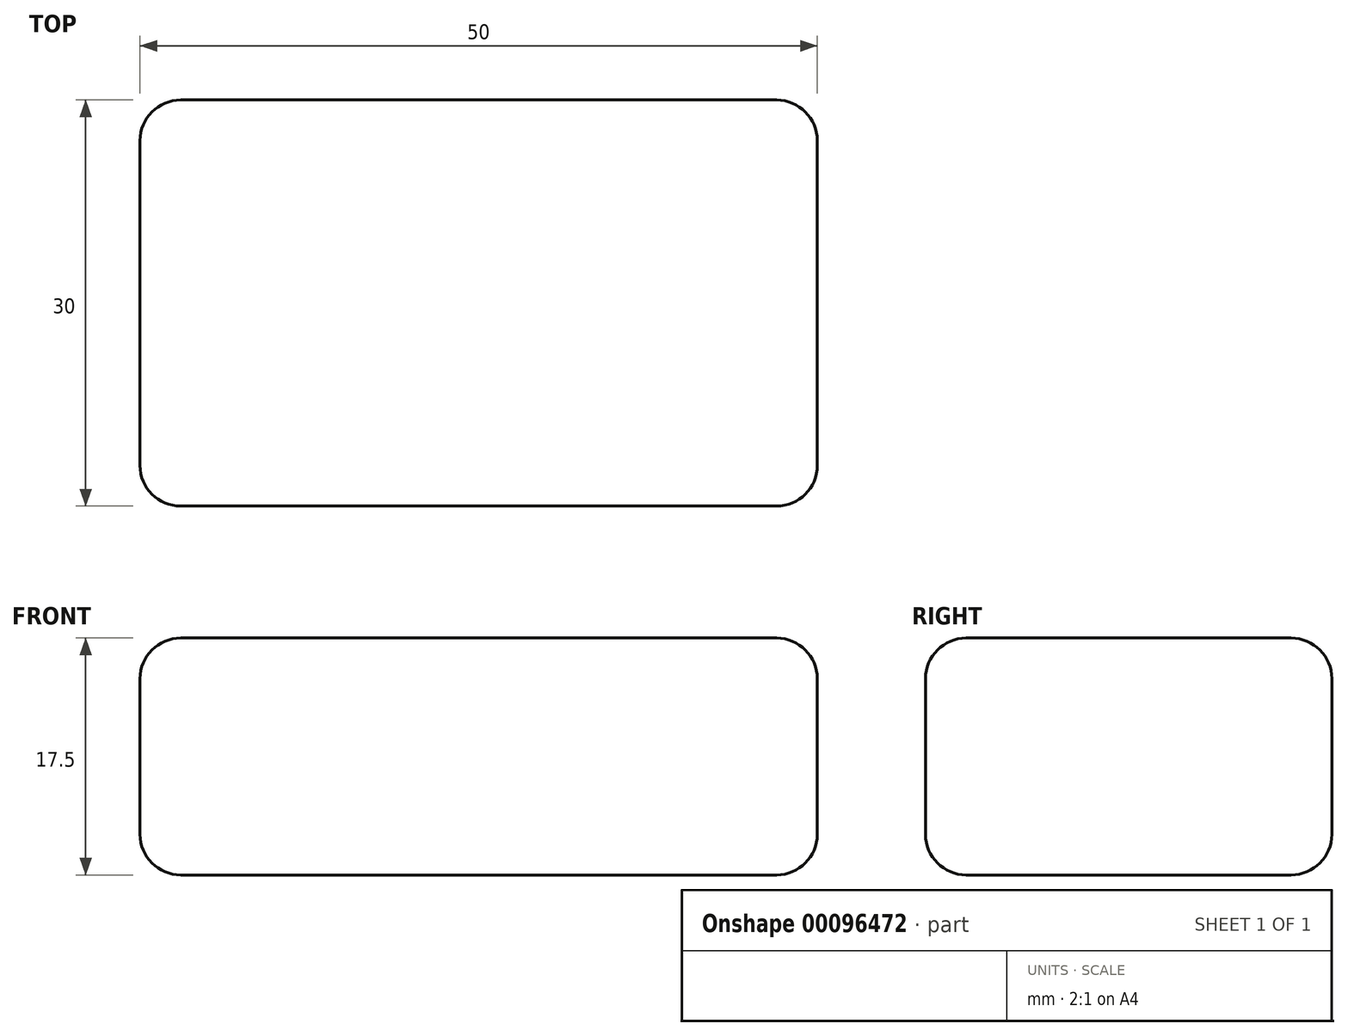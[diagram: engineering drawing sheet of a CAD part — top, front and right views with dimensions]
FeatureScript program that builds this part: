
annotation { "Feature Type Name" : "Feature", "Feature Type Description" : "" }
export const myFeature = defineFeature(function(context is Context, id is Id, definition is map)
    precondition{}
    {
        {
            var Q0;
            Q0=qCreatedBy(makeId("Top.planeOp"),FACE);
            var sketch = newSketch(context, id + "F0", { "sketchPlane" : qUnion([Q0])});
            skLineSegment(sketch, "E0.bottom", {"start": v(25, -15) * mm, "end": v(-25, -15) * mm});
            skLineSegment(sketch, "E0.top", {"start": v(25, 15) * mm, "end": v(-25, 15) * mm});
            skLineSegment(sketch, "E0.left", {"start": v(25, -15) * mm, "end": v(25, 15) * mm});
            skLineSegment(sketch, "E0.right", {"start": v(-25, -15) * mm, "end": v(-25, 15) * mm});
            skPoint(sketch, "E0.middle", {"position": v(0, 0) * mm});
            skSolve(sketch);
        }
        {
            var Q0;
            Q0=makeQuery(id+"F0.imprint","IMPRINT",FACE,{"disambiguationData":[TD([[makeQuery(id+"F0.imprint","IMPRINT",EDGE,{"derivedFrom":sQuery(id+"F0.wireOp",EDGE,"E0.bottom")}),-1.0]])]});
            extrude(context, id + "F1", {"entities" : qUnion([Q0]), "depth" : 17.5 * mm});
        }
        {
            var Q0;
            Q0=makeQuery(id+"F1.opExtrude","CAP_FACE",FACE,{"disambiguationData":[OSD([sQuery(id+"F0.wireOp",EDGE,"E0.bottom"),sQuery(id+"F0.wireOp",EDGE,"E0.top"),sQuery(id+"F0.wireOp",EDGE,"E0.left"),sQuery(id+"F0.wireOp",EDGE,"E0.right")])],"isStart":false});
            var Q1;
            Q1=makeQuery(id+"F1.opExtrude","SWEPT_FACE",FACE,{"disambiguationData":[OSD([sQuery(id+"F0.wireOp",EDGE,"E0.bottom")])]});
            var Q2;
            Q2=makeQuery(id+"F1.opExtrude","SWEPT_EDGE",EDGE,{"disambiguationData":[OSD([sQuery(id+"F0.wireOp",EDGE,"E0.bottom"),sQuery(id+"F0.wireOp",EDGE,"E0.left")])]});
            var Q3;
            Q3=makeQuery(id+"F1.opExtrude","CAP_FACE",FACE,{"disambiguationData":[OSD([sQuery(id+"F0.wireOp",EDGE,"E0.bottom"),sQuery(id+"F0.wireOp",EDGE,"E0.top"),sQuery(id+"F0.wireOp",EDGE,"E0.left"),sQuery(id+"F0.wireOp",EDGE,"E0.right")])],"isStart":true});
            var Q4;
            Q4=makeQuery(id+"F1.opExtrude","SWEPT_EDGE",EDGE,{"disambiguationData":[OSD([sQuery(id+"F0.wireOp",EDGE,"E0.bottom"),sQuery(id+"F0.wireOp",EDGE,"E0.right")])]});
            var Q5;
            Q5=makeQuery(id+"F1.opExtrude","SWEPT_EDGE",EDGE,{"disambiguationData":[OSD([sQuery(id+"F0.wireOp",EDGE,"E0.top"),sQuery(id+"F0.wireOp",EDGE,"E0.left")])]});
            var Q6;
            Q6=makeQuery(id+"F1.opExtrude","SWEPT_FACE",FACE,{"disambiguationData":[OSD([sQuery(id+"F0.wireOp",EDGE,"E0.top")])]});
            var Q7;
            Q7=makeQuery(id+"F1.opExtrude","SWEPT_FACE",FACE,{"disambiguationData":[OSD([sQuery(id+"F0.wireOp",EDGE,"E0.left")])]});
            var Q8;
            Q8=makeQuery(id+"F1.opExtrude","CAP_EDGE",EDGE,{"disambiguationData":[OSD([sQuery(id+"F0.wireOp",EDGE,"E0.bottom")])],"isStart":true});
            var Q9;
            Q9=makeQuery(id+"F1.opExtrude","SWEPT_FACE",FACE,{"disambiguationData":[OSD([sQuery(id+"F0.wireOp",EDGE,"E0.right")])]});
            var Q10;
            Q10=makeQuery(id+"F1.opExtrude","CAP_EDGE",EDGE,{"disambiguationData":[OSD([sQuery(id+"F0.wireOp",EDGE,"E0.top")])],"isStart":false});
            var Q11;
            Q11=makeQuery(id+"F1.opExtrude","CAP_EDGE",EDGE,{"disambiguationData":[OSD([sQuery(id+"F0.wireOp",EDGE,"E0.left")])],"isStart":true});
            var Q12;
            Q12=makeQuery(id+"F1.opExtrude","CAP_EDGE",EDGE,{"disambiguationData":[OSD([sQuery(id+"F0.wireOp",EDGE,"E0.left")])],"isStart":false});
            var Q13;
            Q13=makeQuery(id+"F1.opExtrude","CAP_EDGE",EDGE,{"disambiguationData":[OSD([sQuery(id+"F0.wireOp",EDGE,"E0.right")])],"isStart":false});
            var Q14;
            Q14=makeQuery(id+"F1.opExtrude","SWEPT_EDGE",EDGE,{"disambiguationData":[OSD([sQuery(id+"F0.wireOp",EDGE,"E0.top"),sQuery(id+"F0.wireOp",EDGE,"E0.right")])]});
            var Q15;
            Q15=makeQuery(id+"F1.opExtrude","CAP_EDGE",EDGE,{"disambiguationData":[OSD([sQuery(id+"F0.wireOp",EDGE,"E0.bottom")])],"isStart":false});
            var Q16;
            Q16=makeQuery(id+"F1.opExtrude","CAP_EDGE",EDGE,{"disambiguationData":[OSD([sQuery(id+"F0.wireOp",EDGE,"E0.top")])],"isStart":true});
            var Q17;
            Q17=makeQuery(id+"F1.opExtrude","CAP_EDGE",EDGE,{"disambiguationData":[OSD([sQuery(id+"F0.wireOp",EDGE,"E0.right")])],"isStart":true});
            fillet(context, id + "F2", {"entities" : qUnion([Q0, Q1, Q2, Q3, Q4, Q5, Q6, Q7, Q8, Q9, Q10, Q11, Q12, Q13, Q14, Q15, Q16, Q17]), "radius" : 3 * mm, "tangentPropagation" : true, "allowEdgeOverflow" : false});
        }
    });
